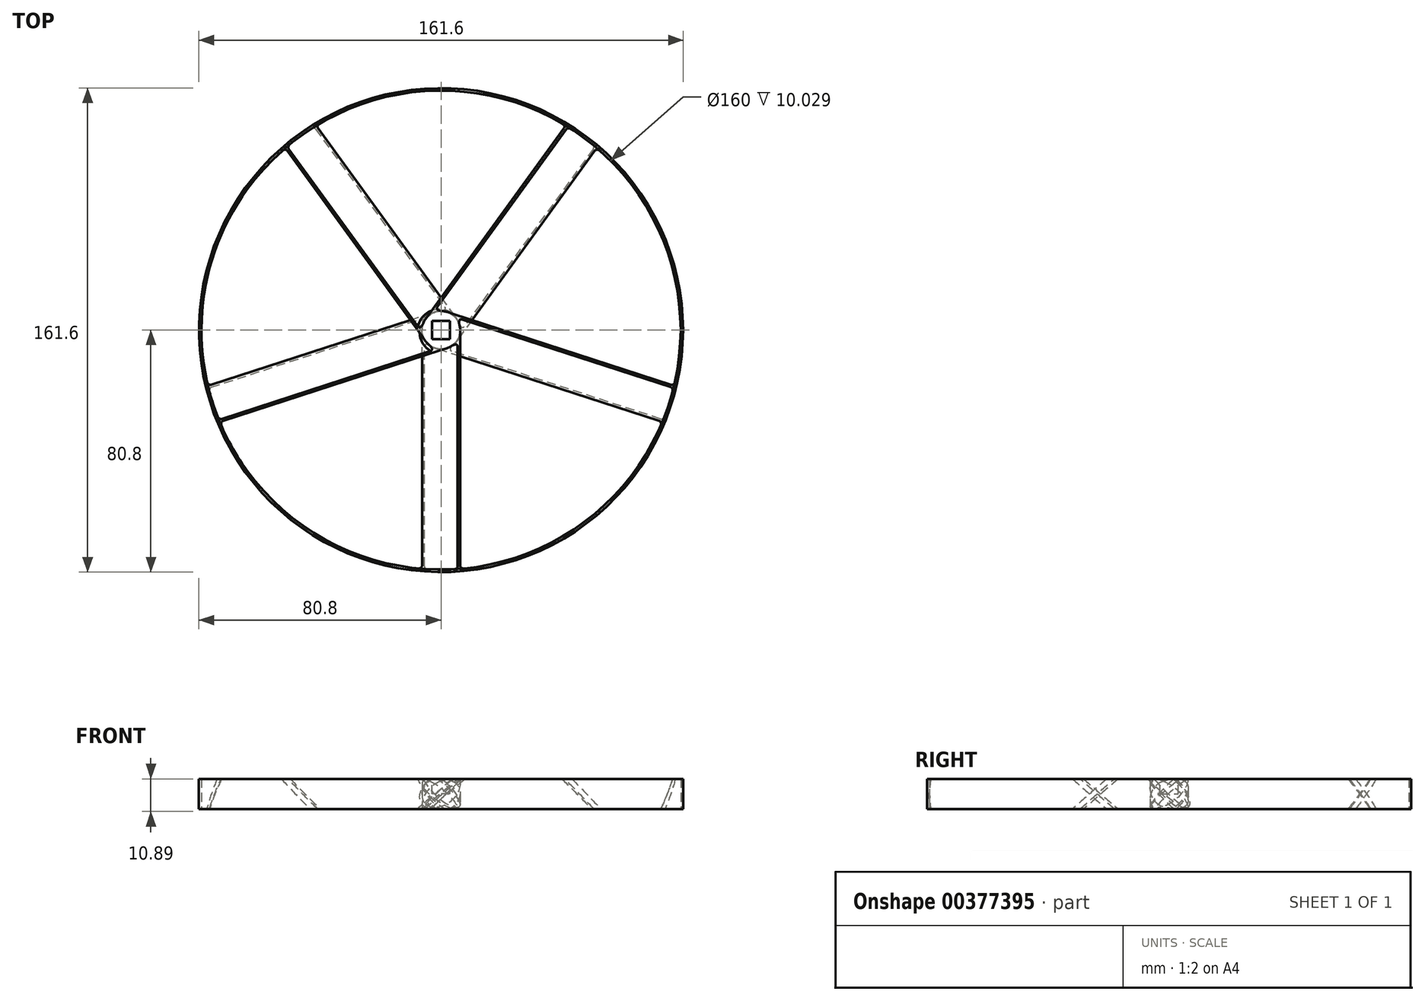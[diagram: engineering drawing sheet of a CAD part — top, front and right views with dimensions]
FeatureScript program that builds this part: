
annotation { "Feature Type Name" : "Feature", "Feature Type Description" : "" }
export const myFeature = defineFeature(function(context is Context, id is Id, definition is map)
    precondition{}
    {
        {
            var Q0;
            Q0=qCreatedBy(makeId("Front.planeOp"),FACE);
            var sketch = newSketch(context, id + "F0", { "sketchPlane" : qUnion([Q0])});
            skLineSegment(sketch, "E0", {"start": v(0, 0) * mm, "end": v(0, 10) * mm, "construction": true});
            skLineSegment(sketch, "E1", {"start": v(0, 0) * mm, "end": v(-5.96, 0) * mm, "construction": true});
            skPoint(sketch, "E2", {"position": v(0, 5) * mm});
            skLineSegment(sketch, "E3", {"start": v(-5.96, 0) * mm, "end": v(0, 5) * mm, "construction": true});
            skLineSegment(sketch, "E4", {"start": v(0, 5) * mm, "end": v(5.96, 10) * mm, "construction": true});
            skSolve(sketch);
        }
        {
            var Q0;
            Q0=qCreatedBy(makeId("Front.planeOp"),FACE);
            var sketch = newSketch(context, id + "F1", { "sketchPlane" : qUnion([Q0])});
            skLineSegment(sketch, "E5.0", {"start": v(-5.96, 0) * mm, "end": v(0, 5) * mm, "construction": true});
            skLineSegment(sketch, "E6.0", {"start": v(0, 5) * mm, "end": v(5.96, 10) * mm, "construction": true});
            skLineSegment(sketch, "E7", {"start": v(-6.36, 0) * mm, "end": v(-5.56, 0) * mm});
            skLineSegment(sketch, "E8", {"start": v(-6.36, 0) * mm, "end": v(5.56, 10) * mm});
            skLineSegment(sketch, "E9", {"start": v(-5.56, 0) * mm, "end": v(6.36, 10) * mm});
            skLineSegment(sketch, "E10", {"start": v(6.36, 10) * mm, "end": v(5.56, 10) * mm});
            skSolve(sketch);
        }
        {
            var Q0;
            Q0=makeQuery(id+"F1.imprint","IMPRINT",FACE,{"disambiguationData":[TD([[makeQuery(id+"F1.imprint","IMPRINT",EDGE,{"derivedFrom":sQuery(id+"F1.wireOp",EDGE,"E7")}),1.0]])]});
            extrude(context, id + "F2", {"entities" : qUnion([Q0]), "depth" : 80 * mm});
        }
        {
            var Q0;
            Q0=qCreatedBy(makeId("Top.planeOp"),FACE);
            var sketch = newSketch(context, id + "F3", { "sketchPlane" : qUnion([Q0])});
            skCircle(sketch, "E11", {"center": v(0, 0) * mm, "radius": 6.36 * mm});
            skLineSegment(sketch, "E12.0", {"start": v(6.36, -80) * mm, "end": v(6.36, 0) * mm, "construction": true});
            skLineSegment(sketch, "E13", {"start": v(0, 0) * mm, "end": v(0, -80) * mm, "construction": true});
            skCircle(sketch, "E14", {"center": v(0, 0) * mm, "radius": 80 * mm});
            skCircle(sketch, "E15.0", {"center": v(0, 0) * mm, "radius": 80.8 * mm});
            skSolve(sketch);
        }
        {
            var Q0;
            Q0=makeQuery(id+"F3.imprint","IMPRINT",FACE,{"disambiguationData":[TD([[makeQuery(id+"F3.imprint","IMPRINT",EDGE,{"derivedFrom":sQuery(id+"F3.wireOp",EDGE,"E14")}),-1.0]])]});
            var Q1;
            Q1=makeQuery(id+"F3.imprint","IMPRINT",FACE,{"disambiguationData":[TD([[makeQuery(id+"F3.imprint","IMPRINT",EDGE,{"derivedFrom":sQuery(id+"F3.wireOp",EDGE,"E11")}),1.0]])]});
            var Q2;
            Q2=makeQuery(id+"F2.opExtrude","SWEPT_FACE",FACE,{"disambiguationData":[OSD([sQuery(id+"F1.wireOp",EDGE,"E10")])]});
            extrude(context, id + "F4", {"entities" : qUnion([Q0, Q1]), "operationType" : NewBodyOperationType.ADD, "endBound" : BoundingType.UP_TO_SURFACE, "endBoundEntityFace" : qUnion([Q2]), "depth" : 25 * mm});
        }
        {
            var Q0;
            Q0=makeQuery(id+"F4.boolean.opBoolean","INTERSECT",EDGE,{"derivedFrom":[makeQuery(id+"F2.opExtrude","SWEPT_FACE",FACE,{"disambiguationData":[OSD([sQuery(id+"F1.wireOp",EDGE,"E8")])]}),makeQuery(id+"F4.opExtrude","SWEPT_FACE",FACE,{"disambiguationData":[OSD([sQuery(id+"F3.wireOp",EDGE,"E14")])]})]});
            var Q1;
            Q1=makeQuery(id+"F4.boolean.opBoolean","INTERSECT",EDGE,{"derivedFrom":[makeQuery(id+"F2.opExtrude","SWEPT_FACE",FACE,{"disambiguationData":[OSD([sQuery(id+"F1.wireOp",EDGE,"E8")])]}),makeQuery(id+"F4.opExtrude","SWEPT_FACE",FACE,{"disambiguationData":[OSD([sQuery(id+"F3.wireOp",EDGE,"E11")])]})]});
            var Q2;
            Q2=makeQuery(id+"F4.boolean.opBoolean","INTERSECT",EDGE,{"derivedFrom":[makeQuery(id+"F2.opExtrude","SWEPT_FACE",FACE,{"disambiguationData":[OSD([sQuery(id+"F1.wireOp",EDGE,"E9")])]}),makeQuery(id+"F4.opExtrude","SWEPT_FACE",FACE,{"disambiguationData":[OSD([sQuery(id+"F3.wireOp",EDGE,"E11")])]})]});
            var Q3;
            Q3=makeQuery(id+"F4.boolean.opBoolean","INTERSECT",EDGE,{"derivedFrom":[makeQuery(id+"F2.opExtrude","SWEPT_FACE",FACE,{"disambiguationData":[OSD([sQuery(id+"F1.wireOp",EDGE,"E9")])]}),makeQuery(id+"F4.opExtrude","SWEPT_FACE",FACE,{"disambiguationData":[OSD([sQuery(id+"F3.wireOp",EDGE,"E14")])]})]});
            fillet(context, id + "F5", {"entities" : qUnion([Q0, Q1, Q2, Q3]), "radius" : 1 * mm, "tangentPropagation" : true, "allowEdgeOverflow" : false});
        }
        {
            var Q0;
            Q0=makeQuery(id+"F2.opExtrude","SWEPT_BODY",BODY,{"disambiguationData":[OSD([sQuery(id+"F1.wireOp",EDGE,"E7"),sQuery(id+"F1.wireOp",EDGE,"E8"),sQuery(id+"F1.wireOp",EDGE,"E9"),sQuery(id+"F1.wireOp",EDGE,"E10")])]});
            var Q1;
            Q1=sQuery(id+"F0.wireOp",EDGE,"E0");
            circularPattern(context, id + "F6", {"operationType" : NewBodyOperationType.ADD, "entities" : qUnion([Q0]), "axis" : qUnion([Q1]), "angle" : 360 * degree, "instanceCount" : 5, "equalSpace" : true});
        }
        {
            var Q0;
            {var subQ0=sQuery(id+"F1.wireOp",EDGE,"E10");Q0=makeQuery(id+"F4.boolean.opBoolean","MERGE",FACE,{"derivedFrom":[makeQuery(id+"F2.opExtrude","SWEPT_FACE",FACE,{"disambiguationData":[OSD([subQ0])]}),makeQuery(id+"F4.opExtrude","CAP_FACE",FACE,{"disambiguationData":[OSD([subQ0]),ownerDisambiguation([makeQuery(id+"F3.imprint","IMPRINT",EDGE,{"derivedFrom":sQuery(id+"F3.wireOp",EDGE,"E11")})])],"isStart":false}),makeQuery(id+"F4.opExtrude","CAP_FACE",FACE,{"disambiguationData":[OSD([subQ0]),ownerDisambiguation([makeQuery(id+"F3.imprint","IMPRINT",EDGE,{"derivedFrom":sQuery(id+"F3.wireOp",EDGE,"E14")})])],"isStart":false})]});}
            var sketch = newSketch(context, id + "F7", { "sketchPlane" : qUnion([Q0])});
            skLineSegment(sketch, "E16.bottom", {"start": v(3, -3) * mm, "end": v(-3, -3) * mm});
            skLineSegment(sketch, "E16.top", {"start": v(3, 3) * mm, "end": v(-3, 3) * mm});
            skLineSegment(sketch, "E16.left", {"start": v(3, -3) * mm, "end": v(3, 3) * mm});
            skLineSegment(sketch, "E16.right", {"start": v(-3, -3) * mm, "end": v(-3, 3) * mm});
            skPoint(sketch, "E16.middle", {"position": v(0, 0) * mm});
            skSolve(sketch);
        }
        {
            var Q0;
            Q0=makeQuery(id+"F7.imprint","IMPRINT",FACE,{"disambiguationData":[TD([[makeQuery(id+"F7.imprint","IMPRINT",EDGE,{"derivedFrom":sQuery(id+"F7.wireOp",EDGE,"E16.bottom")}),-1.0]])]});
            extrude(context, id + "F8", {"entities" : qUnion([Q0]), "operationType" : NewBodyOperationType.REMOVE, "oppositeDirection" : true, "depth" : 5 * mm});
        }
    });
